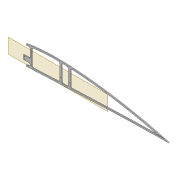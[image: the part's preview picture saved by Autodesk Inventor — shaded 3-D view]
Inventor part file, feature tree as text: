
AUTODESK INVENTOR PART (.ipt)
format: ipt  version: 2022 (Build 260153000, 153)  size: 553,472 bytes
history: native  units: mm
features: sketch x9, projected_geometry x9, extrude x8, fillet x2, shell x1, plane x1, chamfer x1
ambient origin geometry x8: Origin, YZ Plane, XZ Plane, XY Plane, X Axis, Y Axis, Z Axis, Center Point
bodies: Solid1 (feature_tree)
feature tree (31):
  extrude  "Extrusion1"  Depth=4.0mm
  shell  "Shell1"  Thickness=2.0mm
  extrude  "Extrusion8"  Depth=5.9mm
  extrude  "Extrusion3"  Depth=10.0mm TaperAngle=0.0deg
  extrude  "Extrusion4"  Depth=2.0mm
  fillet  "Fillet1"  Radius=5.0mm
  sketch  "Sketch10"  dims[d22=2.0mm d23=0.0mm d31=2.0mm d32=5.0mm]
  extrude  "Extrusion5"  Depth=2.5mm
  plane  "Work Plane2"
  extrude  "Extrusion9"  Depth=1.6mm
  fillet  "Fillet2"  Radius=2.5mm
  extrude  "Extrusion10"  Depth=6.0mm
  chamfer  "Chamfer1"  Distance=2.0mm
  extrude  "Extrusion12"  Depth=12.0mm
  sketch  "Sketch29"  dims[d66=3.0mm d67=12.0mm]
  sketch  "Sketch30"  dims[d68=5.0mm d69=19.0mm d70=12.0mm d71=3.05mm d72=10.0mm d73=0.0mm d74=2.0mm d75=100.0mm d76=20.0mm d77=0.5mm d78=10.0mm d79=0.0mm d82=10.0mm d84=10.0mm d85=3.0mm d86=2.0mm d87=45.0deg d88=1.0mm d89=1.0mm d90=1.0mm d91=1.0mm d92=1.0mm d93=1.0mm d94=10.0mm d95=0.0mm]
  sketch  "Sketch3"  dims[d0=2.0mm d1=0.0mm d2=4.0mm d7=2.0mm]
  sketch  "Sketch8"  dims[d8=2.0mm d9=5.9mm]
  sketch  "Sketch9"  dims[d13=10.0mm d14=0.0mm d16=10.0mm d17=0.0mm]
  projected_geometry  "Projected Loop4"
  projected_geometry  "Projected Loop10"
  sketch  "Sketch24"  dims[d34=1.6mm d35=2.5mm]
  projected_geometry  "Projected Loop11"
  projected_geometry  "Projected Loop12"
  projected_geometry  "Projected Loop13"
  sketch  "Sketch26"  dims[d37=5.0mm d38=1.6mm d40=2.5mm]
  projected_geometry  "Projected Loop14"
  sketch  "Sketch28"  dims[d62=80.0mm d63=6.0mm d64=2.0mm d65=0.0mm]
  projected_geometry  "Project Cut Edges1"
  projected_geometry  "Project Cut Edges2"
  projected_geometry  "Project Cut Edges3"
